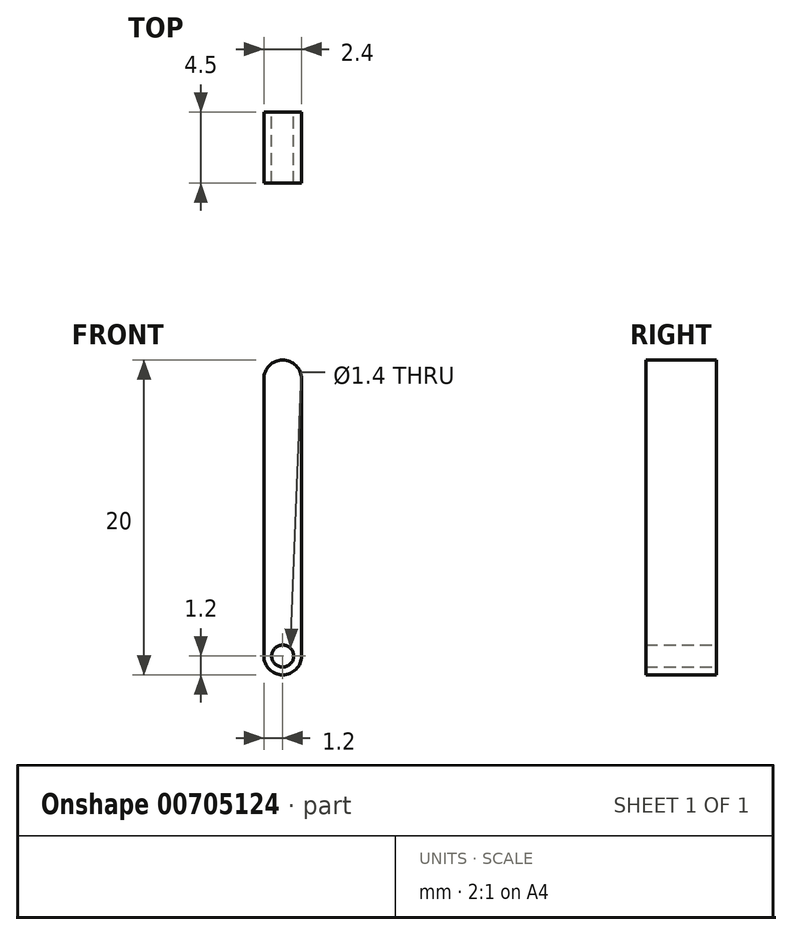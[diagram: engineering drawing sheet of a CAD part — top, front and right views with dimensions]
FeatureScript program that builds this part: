
annotation { "Feature Type Name" : "Feature", "Feature Type Description" : "" }
export const myFeature = defineFeature(function(context is Context, id is Id, definition is map)
    precondition{}
    {
        {
            var Q0;
            Q0=qCreatedBy(makeId("Front.planeOp"),FACE);
            var sketch = newSketch(context, id + "F0", { "sketchPlane" : qUnion([Q0])});
            skLineSegment(sketch, "E0.left", {"start": v(1.2, 0) * mm, "end": v(1.2, 8.8) * mm});
            skLineSegment(sketch, "E0.right", {"start": v(-1.2, 0) * mm, "end": v(-1.2, 8.8) * mm});
            skPoint(sketch, "E0.middle", {"position": v(0, 4.4) * mm});
            skArc(sketch, "E1", {"start": v(1.2, 8.8) * mm, "mid": v(0, 10) * mm, "end": v(-1.2, 8.8) * mm});
            skCircle(sketch, "E2", {"center": v(0, 8.8) * mm, "radius": 0.7 * mm});
            skLineSegment(sketch, "E3.MirrorCS", {"start": v(-1.2, 0) * mm, "end": v(-1.2, -8.8) * mm});
            skArc(sketch, "E4.MirrorCS", {"start": v(1.2, -8.8) * mm, "mid": v(0, -10) * mm, "end": v(-1.2, -8.8) * mm});
            skCircle(sketch, "E5.MirrorC", {"center": v(0, -8.8) * mm, "radius": 0.7 * mm});
            skLineSegment(sketch, "E6.MirrorCS", {"start": v(1.2, 0) * mm, "end": v(1.2, -8.8) * mm});
            skPoint(sketch, "E7.MirrorP", {"position": v(0, -4.4) * mm});
            skSolve(sketch);
        }
        {
            var Q0;
            Q0=makeQuery(id+"F0.imprint","IMPRINT",FACE,{"disambiguationData":[TD([[makeQuery(id+"F0.imprint","IMPRINT",EDGE,{"derivedFrom":sQuery(id+"F0.wireOp",EDGE,"E0.left")}),1.0]])]});
            var Q1;
            Q1=makeQuery(id+"F0.imprint","IMPRINT",FACE,{"disambiguationData":[TD([[makeQuery(id+"F0.imprint","IMPRINT",EDGE,{"derivedFrom":sQuery(id+"F0.wireOp",EDGE,"E2")}),1.0]])]});
            var Q2;
            Q2=makeQuery(id+"F0.imprint","IMPRINT",FACE,{"disambiguationData":[TD([[makeQuery(id+"F0.imprint","IMPRINT",EDGE,{"derivedFrom":sQuery(id+"F0.wireOp",EDGE,"E5.MirrorC")}),-1.0]])]});
            extrude(context, id + "F1", {"entities" : qUnion([Q0, Q1, Q2]), "depth" : 1.5 * mm, "offsetDistance" : 25 * mm});
        }
        {
            var Q0;
            Q0=makeQuery(id+"F0.imprint","IMPRINT",FACE,{"disambiguationData":[TD([[makeQuery(id+"F0.imprint","IMPRINT",EDGE,{"derivedFrom":sQuery(id+"F0.wireOp",EDGE,"E5.MirrorC")}),-1.0]])]});
            var Q1;
            Q1=makeQuery(id+"F0.imprint","IMPRINT",FACE,{"disambiguationData":[TD([[makeQuery(id+"F0.imprint","IMPRINT",EDGE,{"derivedFrom":sQuery(id+"F0.wireOp",EDGE,"E2")}),1.0]])]});
            extrude(context, id + "F2", {"entities" : qUnion([Q0, Q1]), "operationType" : NewBodyOperationType.ADD, "oppositeDirection" : true, "depth" : 3 * mm, "offsetDistance" : 25 * mm});
        }
    });
